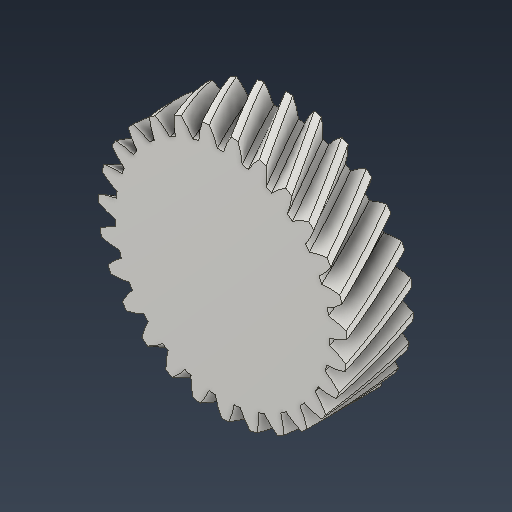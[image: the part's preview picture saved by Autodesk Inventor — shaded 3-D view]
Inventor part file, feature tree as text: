
AUTODESK INVENTOR PART (.ipt)
format: ipt  version: 2022 (Build 260153000, 153)  size: 589,312 bytes
history: native  units: mm (DEFAULTED — no unit token found)
features: plane x3, other x3, sketch x2, extrude x1
ambient origin geometry x8: Origin, YZ Plane, XZ Plane, XY Plane, X Axis, Y Axis, Z Axis, Center Point
bodies: Solid1 (feature_tree)
feature tree (9):
  extrude  "Extrusion1"  Depth=20.0mm TaperAngle=0.0deg
  plane  "Work Plane2"
  plane  "Work Plane8"
  plane  "Work Plane9"
  other  "Spur Gear"
  sketch  "Sketch1"  dims[d0=74.648058mm d1=20.0mm d2=0.0mm]
  sketch  "Sketch2"  dims[d3=70.148058mm d4=10.0mm d5=0.0mm d16=104.0mm d17=0.0mm d34=1.163553mm d39=0.0mm d41=0.0mm d43=104.0mm d46=104.0mm d47=0.0mm d48=0.0mm]
  other  "Srf1"
  other  "Pitch Diameter"
